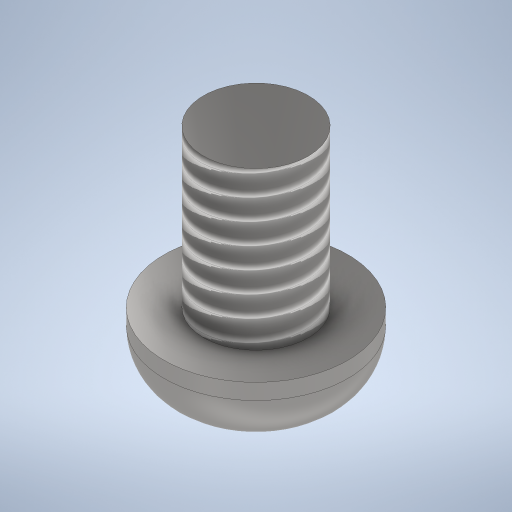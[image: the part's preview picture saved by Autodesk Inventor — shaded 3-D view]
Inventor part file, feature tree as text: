
AUTODESK INVENTOR PART (.ipt)
format: ipt  version: 2024.2 (Build 282272000, 272)  size: 378,880 bytes
history: native  units: mm
features: sketch x2, revolve x2, other x1, thread x1, extrude x1
ambient origin geometry x8: Origin, YZ Plane, XZ Plane, XY Plane, X Axis, Y Axis, Z Axis, Center Point
bodies: Body1 (feature_tree)
feature tree (7):
  other  "ソリッド1"
  sketch  "スケッチ1"
  revolve  "回転1"
  thread  "ねじ1"
  extrude  "押し出し2"  Depth=1.3mm
  revolve  "回転2"
  sketch  "スケッチ2"
